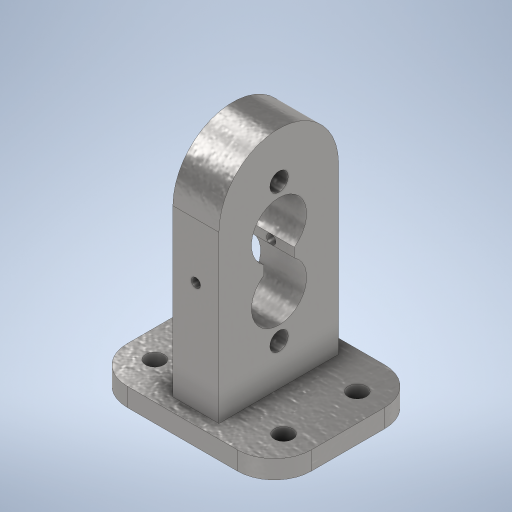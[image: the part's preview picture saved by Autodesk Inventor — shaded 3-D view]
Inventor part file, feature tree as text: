
AUTODESK INVENTOR PART (.ipt)
format: ipt  version: 2024 (Build 280153000, 153)  size: 365,056 bytes
history: native  units: mm
features: sketch x7, extrude x4, hole x3, plane x2, fillet x1
ambient origin geometry x8: Origin, YZ Plane, XZ Plane, XY Plane, X Axis, Y Axis, Z Axis, Center Point
bodies: Volumenkörper1 (feature_tree)
feature tree (17):
  extrude  "Extrusion1"  Depth=10.0mm
  plane  "Arbeitsebene2"
  extrude  "Extrusion2"  Depth=1.0mm
  extrude  "Extrusion3"  Depth=10.0mm
  hole  "Bohrung1"  [1 undecoded]
  hole  "Bohrung2"  [1 undecoded]
  plane  "Arbeitsebene3"
  extrude  "Extrusion4"  Depth=2.5mm TaperAngle=0.0deg
  fillet  "Rundung1"  Radius=0.75mm
  hole  "Bohrung3"  [1 undecoded]
  sketch  "Skizze1"  dims[d0=8.0mm d1=10.0mm]
  sketch  "Skizze3"  dims[d2=1.0mm d3=0.0mm d4=5.0mm]
  sketch  "Skizze4"  dims[d5=6.5mm d6=10.0mm]
  sketch  "Skizze5"  dims[d7=2.5mm d8=0.0mm d9=1.5mm]
  sketch  "Skizze6"  dims[d10=0.5mm d11=4.5mm]
  sketch  "Skizze7"  dims[d12=3.0mm d13=2.5mm d14=0.0mm d15=0.75mm]
  sketch  "Skizze8"  dims[d16=1.0mm d17=6.0mm d18=4.0mm d19=2.0mm d20=90.0deg d21=8.0mm d22=20.594885mm d23=0.75mm d24=1.0mm d25=6.0mm d26=4.0mm d27=2.0mm d28=90.0deg d29=8.0mm d30=20.594885mm d31=4.0mm d32=0.507173mm d33=0.0mm d34=0.0mm d35=2.0mm d36=7.0mm d37=4.0mm d38=1.0mm d39=6.0mm d40=4.0mm d41=2.0mm d42=90.0deg d43=8.0mm d44=20.594885mm]
note: 3 required parameter values undecoded (feature->parameter linkage not recoverable at this tier; creation-order binding heuristic only, values carry confidence <= 0.55)
